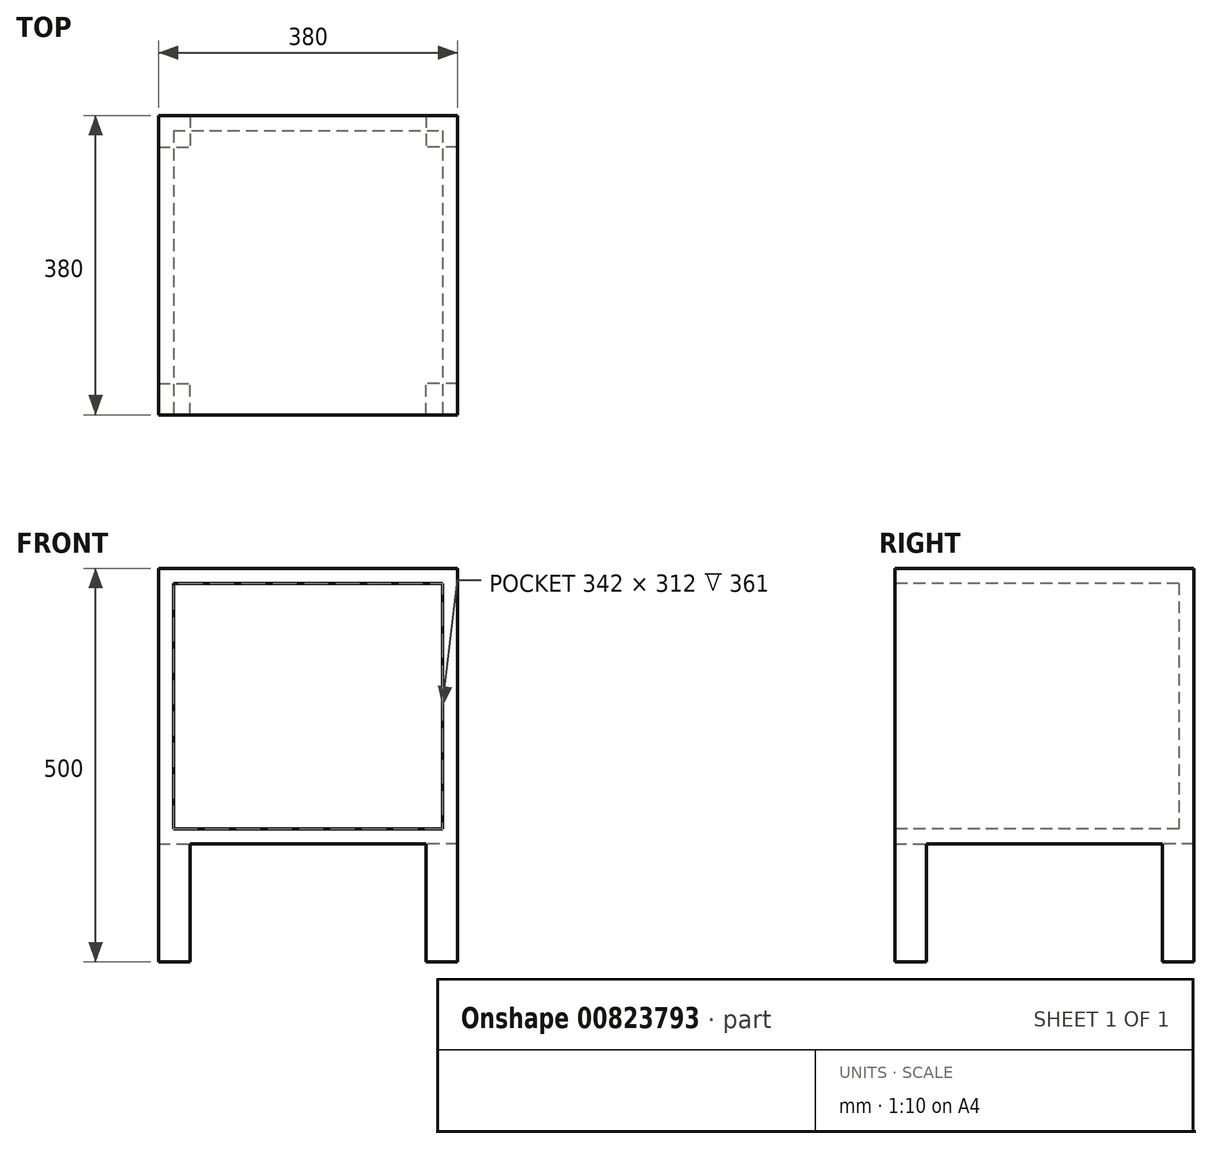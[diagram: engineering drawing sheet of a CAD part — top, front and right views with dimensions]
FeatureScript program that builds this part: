
annotation { "Feature Type Name" : "Feature", "Feature Type Description" : "" }
export const myFeature = defineFeature(function(context is Context, id is Id, definition is map)
    precondition{}
    {
        {
            var Q0;
            Q0=qCreatedBy(makeId("Top.planeOp"),FACE);
            var sketch = newSketch(context, id + "F0", { "sketchPlane" : qUnion([Q0])});
            skLineSegment(sketch, "E0.bottom", {"start": v(190, -190) * mm, "end": v(-190, -190) * mm});
            skLineSegment(sketch, "E0.top", {"start": v(190, 190) * mm, "end": v(-190, 190) * mm});
            skLineSegment(sketch, "E0.left", {"start": v(190, -190) * mm, "end": v(190, 190) * mm});
            skLineSegment(sketch, "E0.right", {"start": v(-190, -190) * mm, "end": v(-190, 190) * mm});
            skPoint(sketch, "E0.middle", {"position": v(0, 0) * mm});
            skSolve(sketch);
        }
        {
            var Q0;
            Q0=makeQuery(id+"F0.imprint","IMPRINT",FACE,{"disambiguationData":[TD([[makeQuery(id+"F0.imprint","IMPRINT",EDGE,{"derivedFrom":sQuery(id+"F0.wireOp",EDGE,"E0.bottom")}),-1.0]])]});
            extrude(context, id + "F1", {"entities" : qUnion([Q0]), "depth" : 350 * mm, "offsetDistance" : 25 * mm});
        }
        {
            var Q0;
            Q0=makeQuery(id+"F1.opExtrude","SWEPT_FACE",FACE,{"disambiguationData":[OSD([sQuery(id+"F0.wireOp",EDGE,"E0.bottom")])]});
            var sketch = newSketch(context, id + "F2", { "sketchPlane" : qUnion([Q0])});
            skLineSegment(sketch, "E1.bottom", {"start": v(-171, 331) * mm, "end": v(171, 331) * mm});
            skLineSegment(sketch, "E1.top", {"start": v(-171, 19) * mm, "end": v(171, 19) * mm});
            skLineSegment(sketch, "E1.left", {"start": v(-171, 331) * mm, "end": v(-171, 19) * mm});
            skLineSegment(sketch, "E1.right", {"start": v(171, 331) * mm, "end": v(171, 19) * mm});
            skSolve(sketch);
        }
        {
            var Q0;
            Q0 = qSketchRegion(id + "F2", true);
            extrude(context, id + "F3", {"entities" : qUnion([Q0]), "operationType" : NewBodyOperationType.REMOVE, "oppositeDirection" : true, "depth" : 361 * mm, "offsetDistance" : 25 * mm});
        }
        {
            var Q0;
            Q0=makeQuery(id+"F1.opExtrude","CAP_FACE",FACE,{"disambiguationData":[OSD([sQuery(id+"F0.wireOp",EDGE,"E0.bottom"),sQuery(id+"F0.wireOp",EDGE,"E0.top"),sQuery(id+"F0.wireOp",EDGE,"E0.left"),sQuery(id+"F0.wireOp",EDGE,"E0.right")])],"isStart":true});
            var sketch = newSketch(context, id + "F4", { "sketchPlane" : qUnion([Q0])});
            skLineSegment(sketch, "E2.bottom", {"start": v(190, 190) * mm, "end": v(150, 190) * mm});
            skLineSegment(sketch, "E2.top", {"start": v(190, 150) * mm, "end": v(150, 150) * mm});
            skLineSegment(sketch, "E2.left", {"start": v(190, 190) * mm, "end": v(190, 150) * mm});
            skLineSegment(sketch, "E2.right", {"start": v(150, 190) * mm, "end": v(150, 150) * mm});
            skLineSegment(sketch, "E3.bottom", {"start": v(-190, 190) * mm, "end": v(-150, 190) * mm});
            skLineSegment(sketch, "E3.top", {"start": v(-190, 150) * mm, "end": v(-150, 150) * mm});
            skLineSegment(sketch, "E3.left", {"start": v(-190, 190) * mm, "end": v(-190, 150) * mm});
            skLineSegment(sketch, "E3.right", {"start": v(-150, 190) * mm, "end": v(-150, 150) * mm});
            skLineSegment(sketch, "E4.bottom", {"start": v(-190, -190) * mm, "end": v(-150, -190) * mm});
            skLineSegment(sketch, "E4.top", {"start": v(-190, -150) * mm, "end": v(-150, -150) * mm});
            skLineSegment(sketch, "E4.left", {"start": v(-190, -190) * mm, "end": v(-190, -150) * mm});
            skLineSegment(sketch, "E4.right", {"start": v(-150, -190) * mm, "end": v(-150, -150) * mm});
            skLineSegment(sketch, "E5.bottom", {"start": v(190, -190) * mm, "end": v(150, -190) * mm});
            skLineSegment(sketch, "E5.top", {"start": v(190, -150) * mm, "end": v(150, -150) * mm});
            skLineSegment(sketch, "E5.left", {"start": v(190, -190) * mm, "end": v(190, -150) * mm});
            skLineSegment(sketch, "E5.right", {"start": v(150, -190) * mm, "end": v(150, -150) * mm});
            skSolve(sketch);
        }
        {
            var Q0;
            Q0=makeQuery(id+"F4.imprint","IMPRINT",FACE,{"disambiguationData":[TD([[makeQuery(id+"F4.imprint","IMPRINT",EDGE,{"derivedFrom":sQuery(id+"F4.wireOp",EDGE,"E2.bottom")}),1.0]])]});
            var Q1;
            Q1=makeQuery(id+"F4.imprint","IMPRINT",FACE,{"disambiguationData":[TD([[makeQuery(id+"F4.imprint","IMPRINT",EDGE,{"derivedFrom":sQuery(id+"F4.wireOp",EDGE,"E3.bottom")}),1.0]])]});
            var Q2;
            Q2=makeQuery(id+"F4.imprint","IMPRINT",FACE,{"disambiguationData":[TD([[makeQuery(id+"F4.imprint","IMPRINT",EDGE,{"derivedFrom":sQuery(id+"F4.wireOp",EDGE,"E5.bottom")}),-1.0]])]});
            var Q3;
            Q3=makeQuery(id+"F4.imprint","IMPRINT",FACE,{"disambiguationData":[TD([[makeQuery(id+"F4.imprint","IMPRINT",EDGE,{"derivedFrom":sQuery(id+"F4.wireOp",EDGE,"E4.bottom")}),-1.0]])]});
            extrude(context, id + "F5", {"entities" : qUnion([Q0, Q1, Q2, Q3]), "operationType" : NewBodyOperationType.ADD, "depth" : 150 * mm, "offsetDistance" : 25 * mm});
        }
    });
